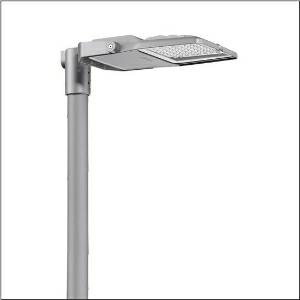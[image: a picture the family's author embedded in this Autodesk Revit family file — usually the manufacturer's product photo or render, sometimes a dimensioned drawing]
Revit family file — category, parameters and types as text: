
# Revit family: floodlight_fl_21_mini___pl64_5xa7776d2e3a_9c1a
name_source: partatom
category: Lighting Fixtures
units: mm (PartAtom-declared; Revit-internal decimal feet)

## family parameters
Cut with Voids When Loaded = No
Host = Face
Light Source = No
Part Type = Normal
Room Calculation Point = No
Round Connector Dimension = Use Diameter
Shared = No

## types (1)
- --- (1 x LED, 17220 lm, 142.9 W, 3000K)
    Apparent Load = 143 VA
    CIE Flux Codes = 28 80 98 100 100
    Color Rendering = 70
    Color Temperature = 3000K
    Default Elevation = 1800 mm
    Description = Floodlight FL 21 mini, floodlight, primary light control with lens, of PMMA, primary optical cover: protective disc, of toughened safety glass, transparent, light distribution: PL64, light emission: direct distribution, installation type: surface-mounted, LED, High Power LED, rated luminous flux: 17.220lm, luminous efficacy: 121lm/W, light colour: 730, colour temperature: 3000K, control gear: Smart Interface (Zhaga), control: flexible luminous flux parameterisation, time-dependent luminous flux control, constant luminous flux control, overheat protection, pre-setting: logarithmic dimming characteristic, with terminal, 6-pole, mains connection: 220..240V, AC, 50/60Hz, start of lifetime: 143W, end of service life: 151W, reduction: 63W, luminaire housing, of diecast aluminium, powder-coated, Siteco® metallic grey (DB 702S), corrosivity category C5 mid according to DIN EN ISO 12944, suitable for swimming pools, chlorine-resistant, sealing non-destructively replaceable, please order mast flange separately, mast bracket, of steel, galvanised, powder-coated, Siteco® metallic grey (DB 702S), Smart Interface below and above, protection rating (complete): IP66, insulation class (complete): insulation class II (safety insulation), certification: CE, ENEC, VDE, protection symbol: D, impact resistance: IK08, permissible operating ambient temperature: -40..+40°C, permissible operating ambient temperature for outdoor applications: -40..+50°C, standard: DIN EN 12944, LABS conformity tested according to VDMA 24364:2018-05, packaging unit: 1 piece

Light Distribution: PL64
    Height = 70 mm
    Lamp = 1 x LED
    Lamp Light Flux = 17220 lm
    Lamp Power = 142.9 W
    Lamp count = 1
    Length = 485 mm
    Luminous efficacy = 121 lm/W
    Manufacturer = Siteco
    ModVariant = No
    Model = 5XA7776D2E3A
    Number of Poles = 1
    OnlyDefault = Yes
    Power Factor = 1
    Product Name = Floodlight FL 21 mini | PL64
    Product group = floodlight | pylon annexe
    ProductGroupID = 6200
    Protection Class = Protection class II
    Protection Degree = IP 66
    RLX_Detail_Level = 1
    RLX_Emergency_Light_Flux = 0 lm
    RLX_Emergency_Type = 0
    RLX_Emergency_Type_DB = No
    RlxData = <blob elided: 101325 chars, md5=4973a484>
    Socket = socket
    Standby Power = 0 W
    System Light Flux = 17220 lm
    System Power = 143 W
    Type Comments = factory setting: luminous flux: 100 % | dim-lin: 254 | 730 mA
    Type Image = l_1007125.jpg
    URL = http://relux.com
    VarID = @adj_165204
    Voltage = 0 V
    Weight = 0.00 kg
    Width = 337 mm

## geometry (parser evidence)
native form markers: Blend x4, Sweep x11
no freeform markers — native parametric forms only
